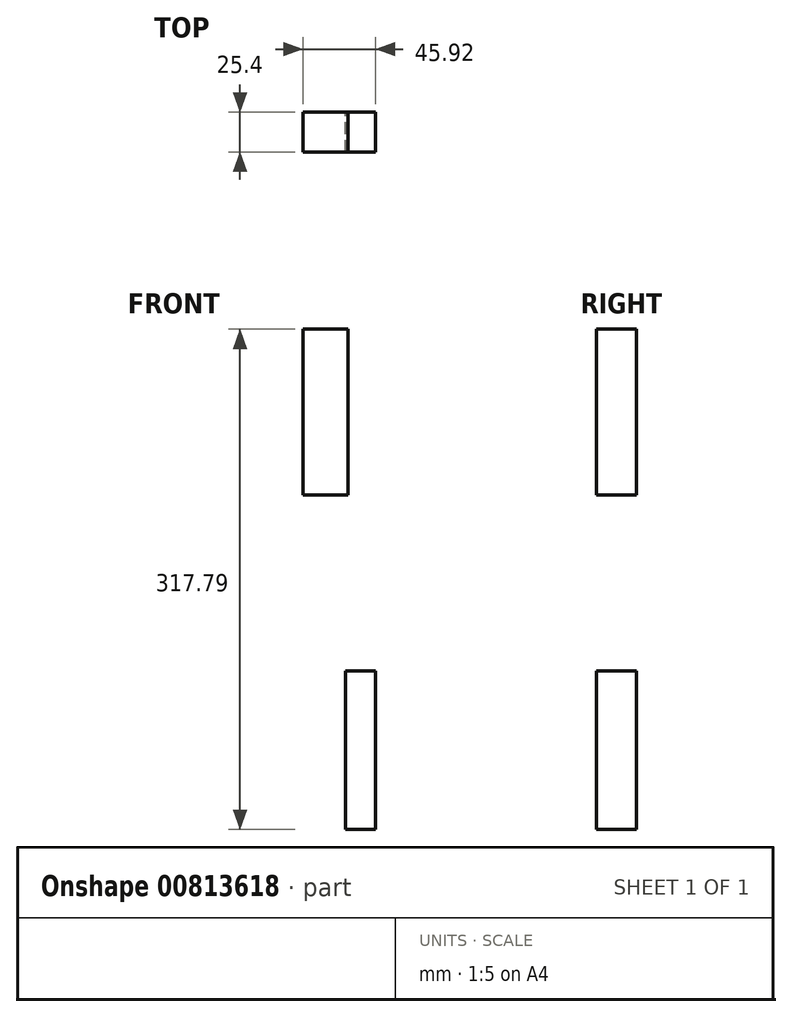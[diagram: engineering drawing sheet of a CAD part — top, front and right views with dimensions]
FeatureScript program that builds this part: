
annotation { "Feature Type Name" : "Feature", "Feature Type Description" : "" }
export const myFeature = defineFeature(function(context is Context, id is Id, definition is map)
    precondition{}
    {
        {
            var Q0;
            Q0=qCreatedBy(makeId("Front.planeOp"),FACE);
            var sketch = newSketch(context, id + "F0", { "sketchPlane" : qUnion([Q0])});
            skLineSegment(sketch, "E0.bottom", {"start": v(-42.43, -10.5) * mm, "end": v(-70.99, -10.5) * mm});
            skLineSegment(sketch, "E0.top", {"start": v(-42.43, 94.84) * mm, "end": v(-70.99, 94.84) * mm});
            skLineSegment(sketch, "E0.left", {"start": v(-42.43, -10.5) * mm, "end": v(-42.43, 94.84) * mm});
            skLineSegment(sketch, "E0.right", {"start": v(-70.99, -10.5) * mm, "end": v(-70.99, 94.84) * mm});
            skPoint(sketch, "E0.middle", {"position": v(-56.71, 42.17) * mm});
            skLineSegment(sketch, "E1.bottom", {"start": v(-25.07, -222.95) * mm, "end": v(-44.14, -222.95) * mm});
            skLineSegment(sketch, "E1.top", {"start": v(-25.07, -122.27) * mm, "end": v(-44.14, -122.27) * mm});
            skLineSegment(sketch, "E1.left", {"start": v(-25.07, -222.95) * mm, "end": v(-25.07, -122.27) * mm});
            skLineSegment(sketch, "E1.right", {"start": v(-44.14, -222.95) * mm, "end": v(-44.14, -122.27) * mm});
            skPoint(sketch, "E1.middle", {"position": v(-34.6, -172.61) * mm});
            skSolve(sketch);
        }
        {
            var Q0;
            Q0 = qSketchRegion(id + "F0", true);
            extrude(context, id + "F1", {"entities" : qUnion([Q0]), "depth" : 25.4 * mm, "offsetDistance" : 25.4 * mm});
        }
    });
